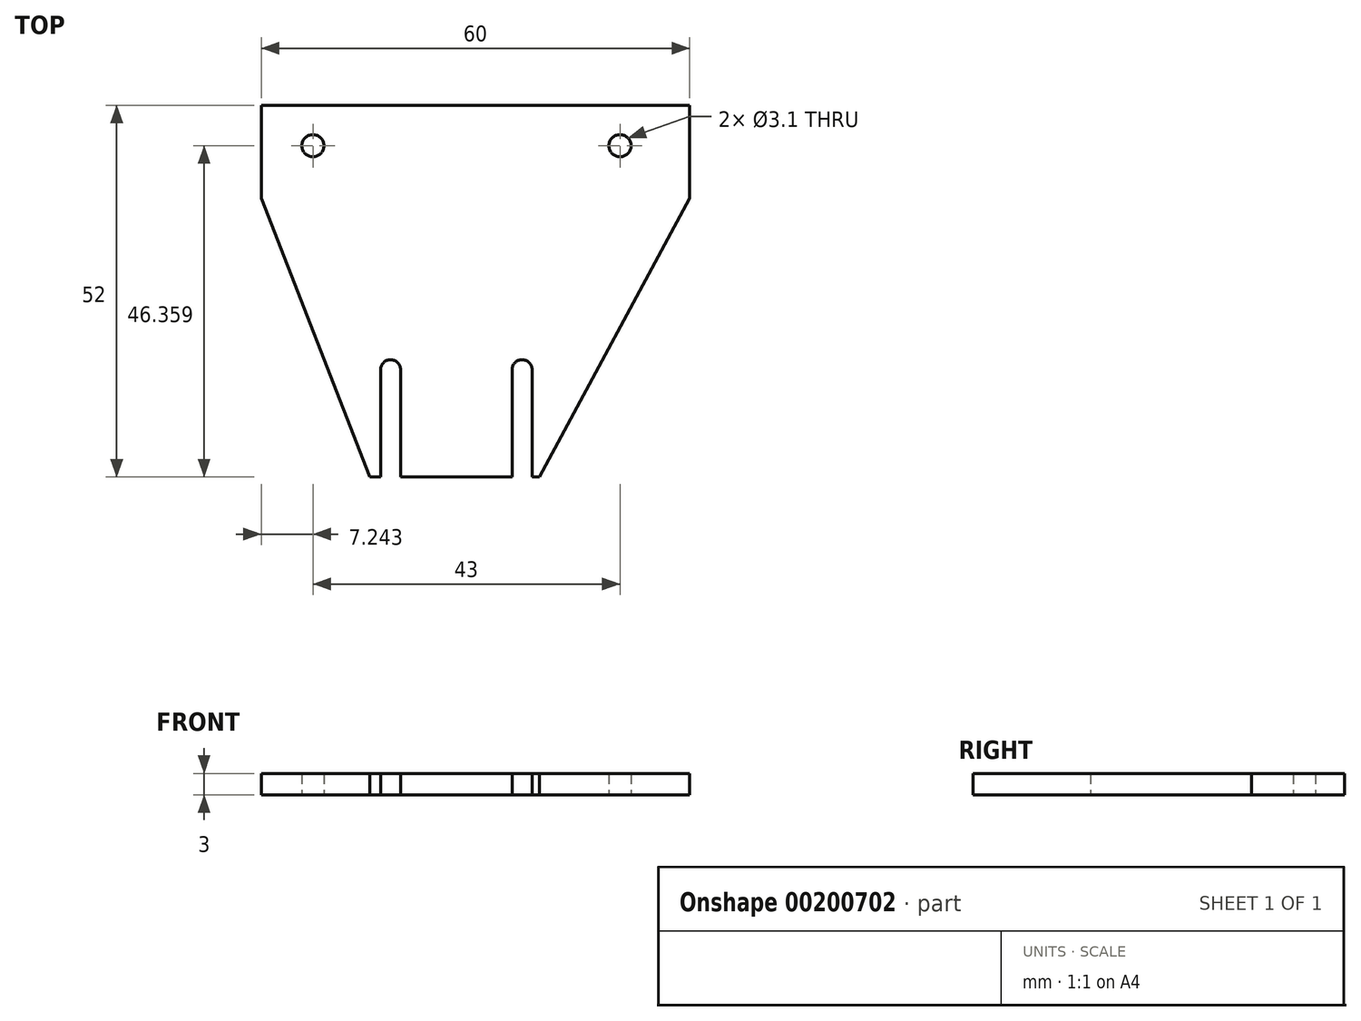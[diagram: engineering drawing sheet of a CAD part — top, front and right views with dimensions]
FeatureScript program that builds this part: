
annotation { "Feature Type Name" : "Feature", "Feature Type Description" : "" }
export const myFeature = defineFeature(function(context is Context, id is Id, definition is map)
    precondition{}
    {
        {
            var Q0;
            Q0=qCreatedBy(makeId("Top.planeOp"),FACE);
            var sketch = newSketch(context, id + "F0", { "sketchPlane" : qUnion([Q0])});
            skLineSegment(sketch, "E0", {"start": v(-38.98, 52) * mm, "end": v(21.02, 52) * mm});
            skLineSegment(sketch, "E1", {"start": v(21.02, 52) * mm, "end": v(21.02, 39) * mm});
            skLineSegment(sketch, "E2", {"start": v(21.02, 39) * mm, "end": v(0, 0) * mm});
            skLineSegment(sketch, "E3", {"start": v(0, 0) * mm, "end": v(-23.76, 0) * mm});
            skLineSegment(sketch, "E4", {"start": v(-23.76, 0) * mm, "end": v(-38.98, 39) * mm});
            skLineSegment(sketch, "E5", {"start": v(-38.98, 39) * mm, "end": v(-38.98, 52) * mm});
            skSolve(sketch);
        }
        {
            var Q0;
            Q0=qCreatedBy(makeId("Top.planeOp"),FACE);
            var sketch = newSketch(context, id + "F1", { "sketchPlane" : qUnion([Q0])});
            skCircle(sketch, "E6", {"center": v(-31.74, 46.36) * mm, "radius": 1.55 * mm});
            skCircle(sketch, "E7", {"center": v(11.26, 46.36) * mm, "radius": 1.55 * mm});
            skSolve(sketch);
        }
        {
            var Q0;
            Q0=makeQuery(id+"F0.imprint","IMPRINT",FACE,{"disambiguationData":[TD([[makeQuery(id+"F0.imprint","IMPRINT",EDGE,{"derivedFrom":sQuery(id+"F0.wireOp",EDGE,"E0")}),-1.0]])]});
            var sketch = newSketch(context, id + "F2", { "sketchPlane" : qUnion([Q0])});
            skLineSegment(sketch, "E8.top", {"start": v(-20.86, 16.4) * mm, "end": v(-20.86, 16.4) * mm});
            skLineSegment(sketch, "E8.left", {"start": v(-22.26, 0) * mm, "end": v(-22.26, 15) * mm});
            skLineSegment(sketch, "E8.right", {"start": v(-19.46, 0) * mm, "end": v(-19.46, 15) * mm});
            skLineSegment(sketch, "E9.bottom", {"start": v(-1.05, 0) * mm, "end": v(-3.85, 0) * mm});
            skLineSegment(sketch, "E9.top", {"start": v(-2.45, 16.4) * mm, "end": v(-2.45, 16.4) * mm});
            skLineSegment(sketch, "E9.left", {"start": v(-1.05, 0) * mm, "end": v(-1.05, 15) * mm});
            skLineSegment(sketch, "E9.right", {"start": v(-3.85, 0) * mm, "end": v(-3.85, 15) * mm});
            skPoint(sketch, "E10.visualSharp", {"position": v(-22.26, 16.4) * mm});
            skArc(sketch, "E10.filletArc", {"start": v(-20.86, 16.4) * mm, "mid": v(-21.85, 15.99) * mm, "end": v(-22.26, 15) * mm});
            skPoint(sketch, "E11.visualSharp", {"position": v(-19.46, 16.4) * mm});
            skArc(sketch, "E11.filletArc", {"start": v(-19.46, 15) * mm, "mid": v(-19.87, 15.99) * mm, "end": v(-20.86, 16.4) * mm});
            skPoint(sketch, "E12.visualSharp", {"position": v(-3.85, 16.4) * mm});
            skArc(sketch, "E12.filletArc", {"start": v(-2.45, 16.4) * mm, "mid": v(-3.44, 15.99) * mm, "end": v(-3.85, 15) * mm});
            skPoint(sketch, "E13.visualSharp", {"position": v(-1.05, 16.4) * mm});
            skArc(sketch, "E13.filletArc", {"start": v(-1.05, 15) * mm, "mid": v(-1.46, 15.99) * mm, "end": v(-2.45, 16.4) * mm});
            skLineSegment(sketch, "E14", {"start": v(-22.26, 0) * mm, "end": v(-19.46, 0) * mm});
            skLineSegment(sketch, "E15", {"start": v(-3.85, 0) * mm, "end": v(-1.05, 0) * mm});
            skLineSegment(sketch, "E16.bottom", {"start": v(-20.86, 0) * mm, "end": v(-2.45, 0) * mm});
            skLineSegment(sketch, "E16.top", {"start": v(-20.86, 0) * mm, "end": v(-2.45, 0) * mm});
            skLineSegment(sketch, "E16.left", {"start": v(-20.86, 0) * mm, "end": v(-20.86, 0) * mm});
            skLineSegment(sketch, "E16.right", {"start": v(-2.45, 0) * mm, "end": v(-2.45, 0) * mm});
            skSolve(sketch);
        }
        {
            var Q0;
            Q0 = qSketchRegion(id + "F0", true);
            extrude(context, id + "F3", {"entities" : qUnion([Q0]), "depth" : 3 * mm});
        }
        {
            var Q0;
            Q0 = qSketchRegion(id + "F1", true);
            extrude(context, id + "F4", {"entities" : qUnion([Q0]), "operationType" : NewBodyOperationType.REMOVE, "depth" : 25 * mm});
        }
        {
            var Q0;
            Q0 = qSketchRegion(id + "F2", true);
            extrude(context, id + "F5", {"entities" : qUnion([Q0]), "operationType" : NewBodyOperationType.REMOVE, "depth" : 25 * mm});
        }
    });
